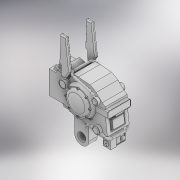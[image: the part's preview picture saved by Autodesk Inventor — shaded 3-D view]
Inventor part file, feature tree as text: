
AUTODESK INVENTOR PART (.ipt)
format: ipt  version: 2022 (Build 260153000, 153)  size: 1,231,360 bytes
history: native  units: mm
features: sketch x39, extrude x35, fillet x6, plane x5, projected_geometry x5, chamfer x4, sweep x3, revolve x2, pattern_circular x2, mirror x2
ambient origin geometry x8: Origin, YZ Plane, XZ Plane, XY Plane, X Axis, Y Axis, Z Axis, Center Point
bodies: Solid1 (feature_tree)
feature tree (103):
  extrude  "Extrusion1"  Depth=3.5mm
  extrude  "Extrusion2"  Depth=3.0mm
  extrude  "Extrusion3"  Depth=4.5mm
  extrude  "Extrusion4"  Depth=2.0mm
  extrude  "Extrusion5"  Depth=1.0mm
  chamfer  "Chamfer1"  Distance=10.5mm
  extrude  "Extrusion6"  Depth=0.75mm TaperAngle=0.0deg
  extrude  "Extrusion7"  Depth=7.0mm
  extrude  "Extrusion8"  Depth=0.75mm
  fillet  "Fillet1"  Radius=0.75mm
  revolve  "Revolution1"  [1 undecoded]
  sketch  "Sketch10"  dims[d14=14.5mm]
  extrude  "Extrusion12"  Depth=0.75mm
  extrude  "Extrusion9"  Depth=0.75mm
  extrude  "Extrusion10"  Depth=0.75mm
  pattern_circular  "Circular Pattern1"  [2 undecoded]
  extrude  "Extrusion11"  Depth=0.75mm TaperAngle=0.0deg
  fillet  "Fillet2"  Radius=11.0mm
  fillet  "Fillet3"  Radius=3.5mm
  extrude  "Extrusion13"  Depth=0.5mm
  extrude  "Extrusion14"  Depth=0.5mm
  extrude  "Extrusion15"  Depth=0.5mm
  pattern_circular  "Circular Pattern2"  [2 undecoded]
  sketch  "Sketch18"  dims[d20=3.348045mm]
  extrude  "Extrusion16"  Depth=0.75mm TaperAngle=0.0deg
  extrude  "Extrusion17"  Depth=0.75mm TaperAngle=0.0deg
  extrude  "Extrusion18"  Depth=0.5mm TaperAngle=45.0deg
  extrude  "Extrusion19"  Depth=0.75mm
  extrude  "Extrusion20"  Depth=0.75mm
  extrude  "Extrusion21"  Depth=0.75mm TaperAngle=0.0deg
  extrude  "Extrusion22"  Depth=0.75mm
  extrude  "Extrusion23"  Depth=0.75mm
  plane  "Work Plane1"
  revolve  "Revolution2"  [1 undecoded]
  extrude  "Extrusion24"  Depth=0.75mm
  extrude  "Extrusion25"  Depth=10.0mm TaperAngle=0.0deg
  extrude  "Extrusion26"  Depth=0.5mm
  extrude  "Extrusion27"  Depth=0.75mm
  extrude  "Extrusion28"  Depth=0.75mm
  plane  "Work Plane2"
  sketch  "Sketch29"  dims[d32=9.0mm]
  extrude  "Extrusion29"  Depth=0.75mm
  fillet  "Fillet4"  Radius=2.0mm
  chamfer  "Chamfer2"  Distance=2.0mm
  fillet  "Fillet5"  Radius=1.0mm
  plane  "Work Plane3"
  sweep  "Sweep1"
  sketch  "Sketch32"  dims[d34=10.0mm]
  extrude  "Extrusion30"  Depth=0.5mm
  extrude  "Extrusion31"  TaperAngle=90.0deg  [1 undecoded]
  sketch  "Sketch33"  dims[d35=9.5mm]
  chamfer  "Chamfer3"  Distance=15.0mm
  chamfer  "Chamfer4"  Distance=0.4mm
  mirror  "Mirror1"
  plane  "Work Plane4"
  sketch  "Sketch34"  dims[d36=5.0mm]
  sweep  "Sweep3"
  sweep  "Sweep4"
  mirror  "Mirror2"
  sketch  "Sketch37"  dims[d39=8.0mm]
  extrude  "Extrusion32"  Depth=0.75mm TaperAngle=0.0deg
  plane  "Work Plane5"
  extrude  "Extrusion33"  Depth=0.75mm TaperAngle=360.0deg
  fillet  "Fillet6"  Radius=0.9mm
  extrude  "Extrusion34"  Depth=0.5mm
  extrude  "Extrusion35"  Depth=0.5mm
  sketch  "Sketch1"  dims[d0=12.0mm d1=3.5mm]
  sketch  "Sketch2"  dims[d2=12.0mm d3=3.0mm]
  sketch  "Sketch3"  dims[d4=1.0mm d5=4.5mm]
  sketch  "Sketch4"  dims[d6=3.0mm d7=2.0mm]
  sketch  "Sketch5"  dims[d8=1.0mm d9=1.0mm]
  projected_geometry  "Projected Loop1"
  sketch  "Sketch6"  dims[d10=1.5mm]
  sketch  "Sketch7"  dims[d11=7.0mm]
  sketch  "Sketch8"  dims[d12=10.0mm]
  sketch  "Sketch9"  dims[d13=13.0mm]
  sketch  "Sketch11"  dims[d15=14.5mm]
  sketch  "Sketch12"  dims[d16=15.5mm]
  sketch  "Sketch15"  dims[d17=10.5mm]
  sketch  "Sketch16"  dims[d18=11.0mm]
  sketch  "Sketch17"  dims[d19=5.5mm]
  projected_geometry  "Projected Loop3"
  sketch  "Sketch19"  dims[d21=13.0mm]
  projected_geometry  "Projected Loop4"
  sketch  "Sketch20"  dims[d23=3.0mm]
  projected_geometry  "Projected Loop5"
  sketch  "Sketch21"  dims[d24=7.0mm]
  sketch  "Sketch22"  dims[d25=2.0mm]
  sketch  "Sketch23"  dims[d26=7.5mm]
  sketch  "Sketch24"  dims[d27=7.0mm]
  sketch  "Sketch25"  dims[d28=6.0mm]
  sketch  "Sketch26"  dims[d29=6.0mm]
  sketch  "Sketch27"  dims[d30=6.0mm]
  sketch  "Sketch28"  dims[d31=8.5mm]
  sketch  "Sketch31"  dims[d33=10.0mm]
  sketch  "3D Sketch1"
  sketch  "Sketch35"  dims[d37=4.0mm]
  sketch  "3D Sketch6"
  sketch  "Sketch36"  dims[d38=0.0mm]
  sketch  "Sketch38"  dims[d40=10.0mm]
  sketch  "Sketch39"  dims[d41=10.5mm]
  projected_geometry  "Projected Loop6"
  sketch  "Sketch40"  dims[d42=10.0mm d43=10.5mm d44=10.5mm d45=0.0mm d47=7.0mm d48=5.5mm d49=0.75mm d50=0.75mm d51=0.75mm d52=0.75mm d53=1.0mm d54=3.0mm d55=0.0mm d56=3.5mm d57=0.0mm d58=11.0mm d59=3.5mm d60=0.5mm d61=0.5mm d62=0.5mm d65=0.5mm d66=1.5mm d67=5.0mm d68=0.0mm d69=0.0mm d70=0.25mm d71=0.0mm d72=0.5mm d73=2.0mm d74=45.0deg d75=0.25mm d76=0.2mm d77=0.25mm d78=0.0mm d79=5.0mm d80=2.5mm d81=2.0mm d82=0.0mm d83=1.0mm d84=10.0mm d85=0.0mm d86=0.5mm d87=12.0mm d88=14.0mm d89=1.5mm d90=2.0mm d91=2.0mm d93=1.0mm d94=1.5mm d95=0.5mm d96=90.0deg d97=15.0mm d98=0.4mm d99=0.425mm d100=1.0mm d101=0.0mm d102=0.6mm d103=0.0mm d104=80.0mm d105=360.0deg d107=0.9mm d108=0.0mm d109=0.5mm d110=0.5mm d111=0.9mm d112=0.0mm d113=1.3mm d114=2.15mm d115=0.0mm d116=0.5mm d117=1.0mm d118=0.5mm d119=0.0mm d120=0.6mm d121=0.0mm d122=20.0mm d123=1551.248639mm d125=4.5mm d126=0.75mm d127=3.5mm d128=1.5mm d129=0.25mm d130=3.0mm d131=2.5mm d132=0.25mm d133=0.75mm d134=0.75mm d135=3.0mm d136=8.0mm d137=0.0mm d138=7.5mm d139=0.0mm d140=6.75mm d141=0.0mm d142=0.3mm d143=0.25mm d144=0.25mm d145=0.0mm d146=3.25mm d147=3.75mm d148=1.0mm d149=0.2mm d150=0.5mm d151=2.5mm d152=7.5mm d153=0.0mm d154=0.25mm d155=0.0mm d156=0.25mm d157=0.0mm d158=0.25mm d159=0.0mm d160=90.0deg d161=2.5mm d162=0.25mm d163=0.0mm d164=0.1mm d165=0.0mm d166=0.1mm d167=0.0mm d168=3.5mm d169=2.1mm d170=0.0mm d171=0.1mm d172=0.0mm d173=1.5mm d174=0.0mm d175=0.5mm d176=0.5mm d177=2.0mm d178=45.0deg d179=0.5mm d180=1.0mm d181=0.0mm d182=0.0mm d183=3.5mm d184=3.0mm d187=1.3mm d188=0.0mm d189=1.6mm d190=0.0mm d191=0.25mm d192=2.0mm d193=45.0deg d194=0.25mm d195=2.0mm d196=45.0deg d197=2.0mm d198=2.0mm d199=1.0mm d202=0.0mm d203=0.0mm d204=2.0mm d205=2.0mm d206=2.0mm d207=1.0mm d208=0.0mm d209=0.0mm d210=4.0mm d211=7.0mm d212=8.0mm d213=4.0mm d214=0.0mm d217=1.679781mm d218=13.912215mm d219=3.472939mm d220=2.026421mm d221=2.206562mm d222=0.047706mm d223=0.098811mm d224=0.875272mm d225=16.767391mm d226=20.497253mm d227=21.206034mm d228=90.0deg d229=9.0mm d230=10.5mm d231=0.0mm d232=6.0mm d233=10.5mm d234=0.0mm d235=0.75mm d236=0.0mm]
note: 7 required parameter values undecoded (feature->parameter linkage not recoverable at this tier; creation-order binding heuristic only, values carry confidence <= 0.55)